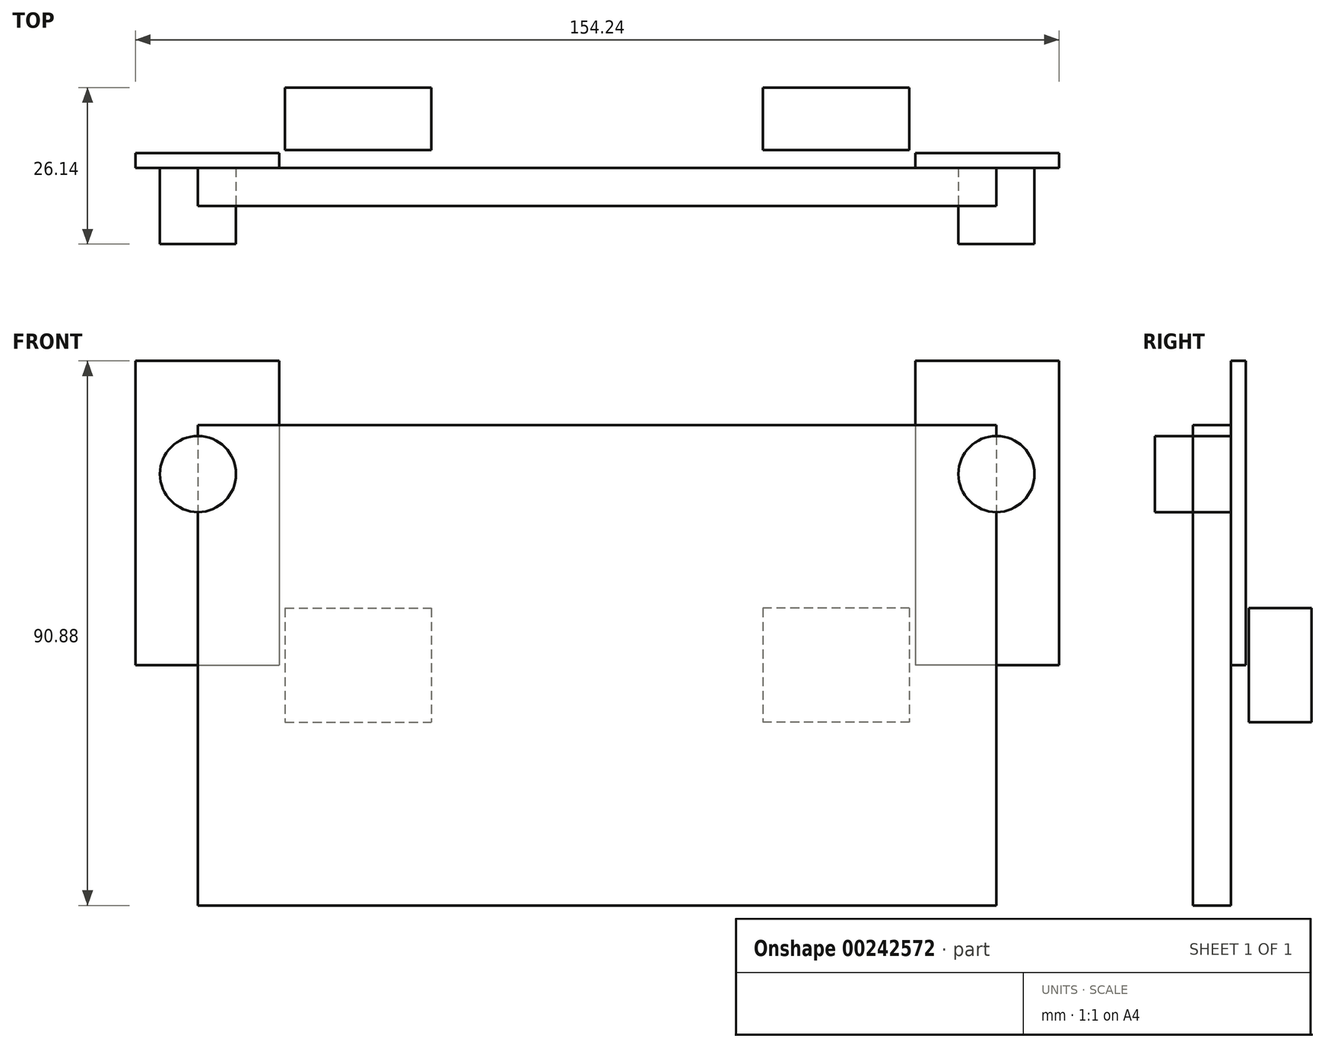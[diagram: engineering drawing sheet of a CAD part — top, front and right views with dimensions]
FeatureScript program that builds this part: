
annotation { "Feature Type Name" : "Feature", "Feature Type Description" : "" }
export const myFeature = defineFeature(function(context is Context, id is Id, definition is map)
    precondition{}
    {
        {
            var Q0;
            Q0=qCreatedBy(makeId("Front.planeOp"),FACE);
            var sketch = newSketch(context, id + "F0", { "sketchPlane" : qUnion([Q0])});
            skLineSegment(sketch, "E0.bottom", {"start": v(66.68, 40.08) * mm, "end": v(-66.68, 40.08) * mm});
            skLineSegment(sketch, "E0.top", {"start": v(66.68, -40.08) * mm, "end": v(-66.68, -40.08) * mm});
            skLineSegment(sketch, "E0.left", {"start": v(66.68, 40.08) * mm, "end": v(66.68, -40.08) * mm});
            skLineSegment(sketch, "E0.right", {"start": v(-66.68, 40.08) * mm, "end": v(-66.68, -40.08) * mm});
            skPoint(sketch, "E0.middle", {"position": v(0, 0) * mm});
            skSolve(sketch);
        }
        {
            var Q0;
            Q0 = qSketchRegion(id + "F0", true);
            extrude(context, id + "F1", {"entities" : qUnion([Q0]), "depth" : 6.35 * mm});
        }
        {
            var Q0;
            Q0=qCreatedBy(makeId("Top.planeOp"),FACE);
            var sketch = newSketch(context, id + "F2", { "sketchPlane" : qUnion([Q0])});
            skLineSegment(sketch, "E1.bottom", {"start": v(-77.12, 0) * mm, "end": v(-53.12, 0) * mm});
            skLineSegment(sketch, "E1.top", {"start": v(-77.12, 2.5) * mm, "end": v(-53.12, 2.5) * mm});
            skLineSegment(sketch, "E1.left", {"start": v(-77.12, 0) * mm, "end": v(-77.12, 2.5) * mm});
            skLineSegment(sketch, "E1.right", {"start": v(-53.12, 0) * mm, "end": v(-53.12, 2.5) * mm});
            skLineSegment(sketch, "E2.MirrorCS", {"start": v(77.12, 0) * mm, "end": v(53.12, 0) * mm});
            skLineSegment(sketch, "E3.MirrorCS", {"start": v(77.12, 0) * mm, "end": v(77.12, 2.5) * mm});
            skLineSegment(sketch, "E4.MirrorCS", {"start": v(77.12, 2.5) * mm, "end": v(53.12, 2.5) * mm});
            skLineSegment(sketch, "E5.MirrorCS", {"start": v(53.12, 0) * mm, "end": v(53.12, 2.5) * mm});
            skSolve(sketch);
        }
        {
            var Q0;
            Q0 = qSketchRegion(id + "F2", true);
            extrude(context, id + "F3", {"entities" : qUnion([Q0]), "depth" : 50.8 * mm});
        }
        {
            var Q0;
            Q0=qCreatedBy(makeId("Top.planeOp"),FACE);
            var sketch = newSketch(context, id + "F4", { "sketchPlane" : qUnion([Q0])});
            skLineSegment(sketch, "E6.bottom", {"start": v(-52.13, 3) * mm, "end": v(-27.69, 3) * mm});
            skLineSegment(sketch, "E6.top", {"start": v(-52.13, 13.44) * mm, "end": v(-27.69, 13.44) * mm});
            skLineSegment(sketch, "E6.left", {"start": v(-52.13, 3) * mm, "end": v(-52.13, 13.44) * mm});
            skLineSegment(sketch, "E6.right", {"start": v(-27.69, 3) * mm, "end": v(-27.69, 13.44) * mm});
            skLineSegment(sketch, "E7.MirrorCS", {"start": v(27.69, 3) * mm, "end": v(27.69, 13.44) * mm});
            skLineSegment(sketch, "E8.MirrorCS", {"start": v(52.13, 3) * mm, "end": v(27.69, 3) * mm});
            skLineSegment(sketch, "E9.MirrorCS", {"start": v(52.13, 3) * mm, "end": v(52.13, 13.44) * mm});
            skLineSegment(sketch, "E10.MirrorCS", {"start": v(52.13, 13.44) * mm, "end": v(27.69, 13.44) * mm});
            skSolve(sketch);
        }
        {
            var Q0;
            Q0 = qSketchRegion(id + "F4", true);
            extrude(context, id + "F5", {"entities" : qUnion([Q0]), "endBound" : BoundingType.SYMMETRIC, "depth" : 19.05 * mm});
        }
        {
            var Q0;
            Q0=makeQuery(id+"F1.opExtrude","CAP_FACE",FACE,{"disambiguationData":[OSD([sQuery(id+"F0.wireOp",EDGE,"E0.bottom"),sQuery(id+"F0.wireOp",EDGE,"E0.top"),sQuery(id+"F0.wireOp",EDGE,"E0.left"),sQuery(id+"F0.wireOp",EDGE,"E0.right")])],"isStart":false});
            var sketch = newSketch(context, id + "F6", { "sketchPlane" : qUnion([Q0])});
            skCircle(sketch, "E11", {"center": v(-66.68, 31.93) * mm, "radius": 6.35 * mm});
            skCircle(sketch, "E12.MirrorC", {"center": v(66.68, 31.93) * mm, "radius": 6.35 * mm});
            skSolve(sketch);
        }
        {
            var Q0;
            Q0 = qSketchRegion(id + "F6", true);
            extrude(context, id + "F7", {"entities" : qUnion([Q0]), "endBound" : BoundingType.SYMMETRIC, "oppositeDirection" : true, "depth" : 12.7 * mm});
        }
    });
